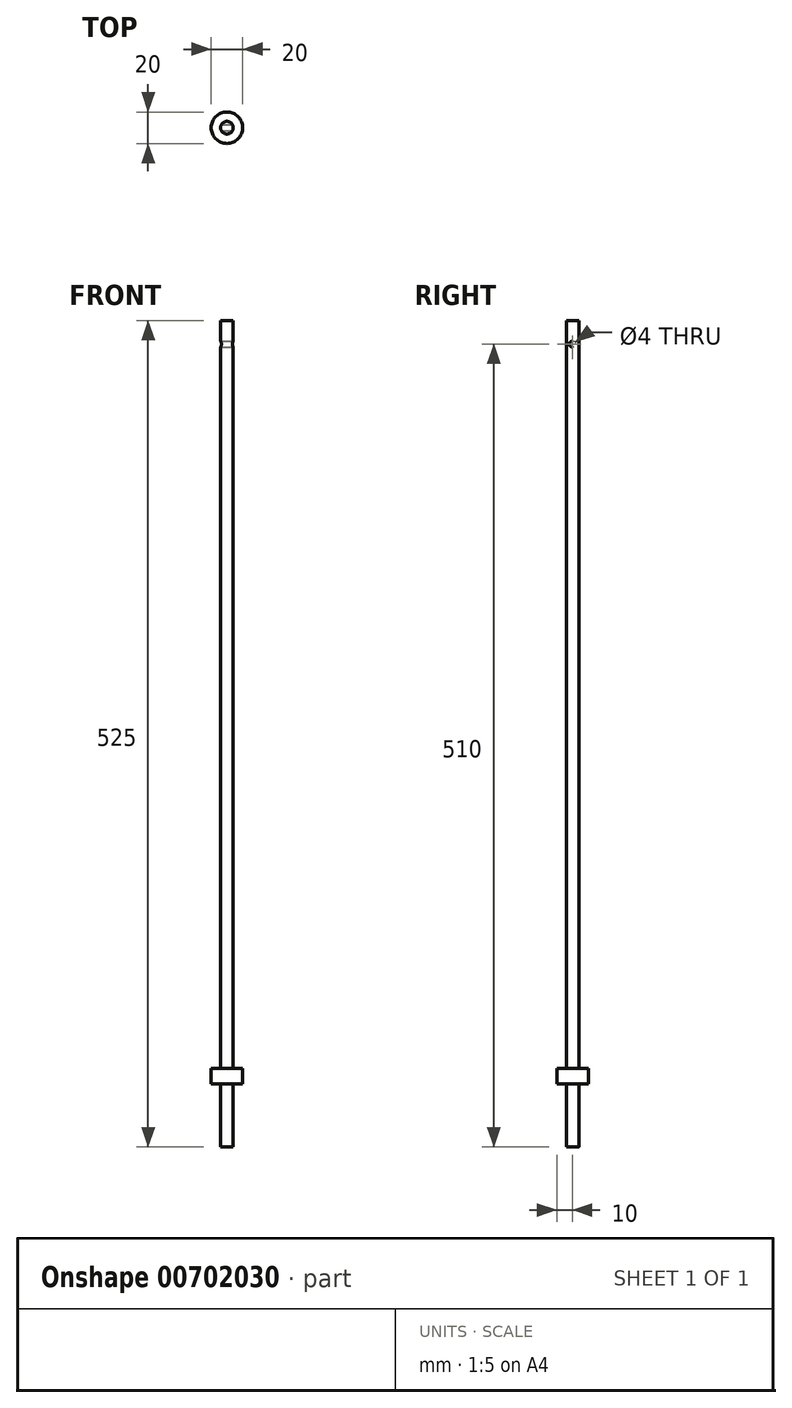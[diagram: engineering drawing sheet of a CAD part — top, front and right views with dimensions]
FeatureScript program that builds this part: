
annotation { "Feature Type Name" : "Feature", "Feature Type Description" : "" }
export const myFeature = defineFeature(function(context is Context, id is Id, definition is map)
    precondition{}
    {
        {
            var Q0;
            Q0=qCreatedBy(makeId("Top.planeOp"),FACE);
            var sketch = newSketch(context, id + "F0", { "sketchPlane" : qUnion([Q0])});
            skCircle(sketch, "E0", {"center": v(0, 0) * mm, "radius": 4 * mm});
            skSolve(sketch);
        }
        {
            var Q0;
            Q0=qSketchRegion(id+"F0",true);
            extrude(context, id + "F1", {"entities" : qUnion([Q0]), "oppositeDirection" : true, "depth" : 500 * mm, "offsetDistance" : 25 * mm});
        }
        {
            var Q0;
            Q0=qCreatedBy(makeId("Top.planeOp"),FACE);
            var sketch = newSketch(context, id + "F2", { "sketchPlane" : qUnion([Q0])});
            skCircle(sketch, "E1", {"center": v(0, 0) * mm, "radius": 10 * mm});
            skCircle(sketch, "E2", {"center": v(0, 0) * mm, "radius": 4 * mm});
            skSolve(sketch);
        }
        {
            var Q0;
            Q0=qSketchRegion(id+"F2",true);
            extrude(context, id + "F3", {"entities" : qUnion([Q0]), "operationType" : NewBodyOperationType.ADD, "oppositeDirection" : true, "depth" : 460 * mm, "offsetDistance" : 25 * mm, "hasSecondDirection" : true, "secondDirectionOppositeDirection" : true, "secondDirectionDepth" : 450 * mm});
        }
        {
            var Q0;
            Q0 = qSketchRegion(id + "F0", true);
            extrude(context, id + "F4", {"entities" : qUnion([Q0]), "operationType" : NewBodyOperationType.ADD, "depth" : 25 * mm, "offsetDistance" : 25 * mm});
        }
        {
            var Q0;
            Q0=qCreatedBy(makeId("Right.planeOp"),FACE);
            var sketch = newSketch(context, id + "F5", { "sketchPlane" : qUnion([Q0])});
            skCircle(sketch, "E3", {"center": v(0, 10) * mm, "radius": 2 * mm});
            skSolve(sketch);
        }
        {
            var Q0;
            Q0 = qSketchRegion(id + "F5", true);
            extrude(context, id + "F6", {"entities" : qUnion([Q0]), "operationType" : NewBodyOperationType.REMOVE, "endBound" : BoundingType.SYMMETRIC, "oppositeDirection" : true, "depth" : 25 * mm, "offsetDistance" : 25 * mm});
        }
    });
